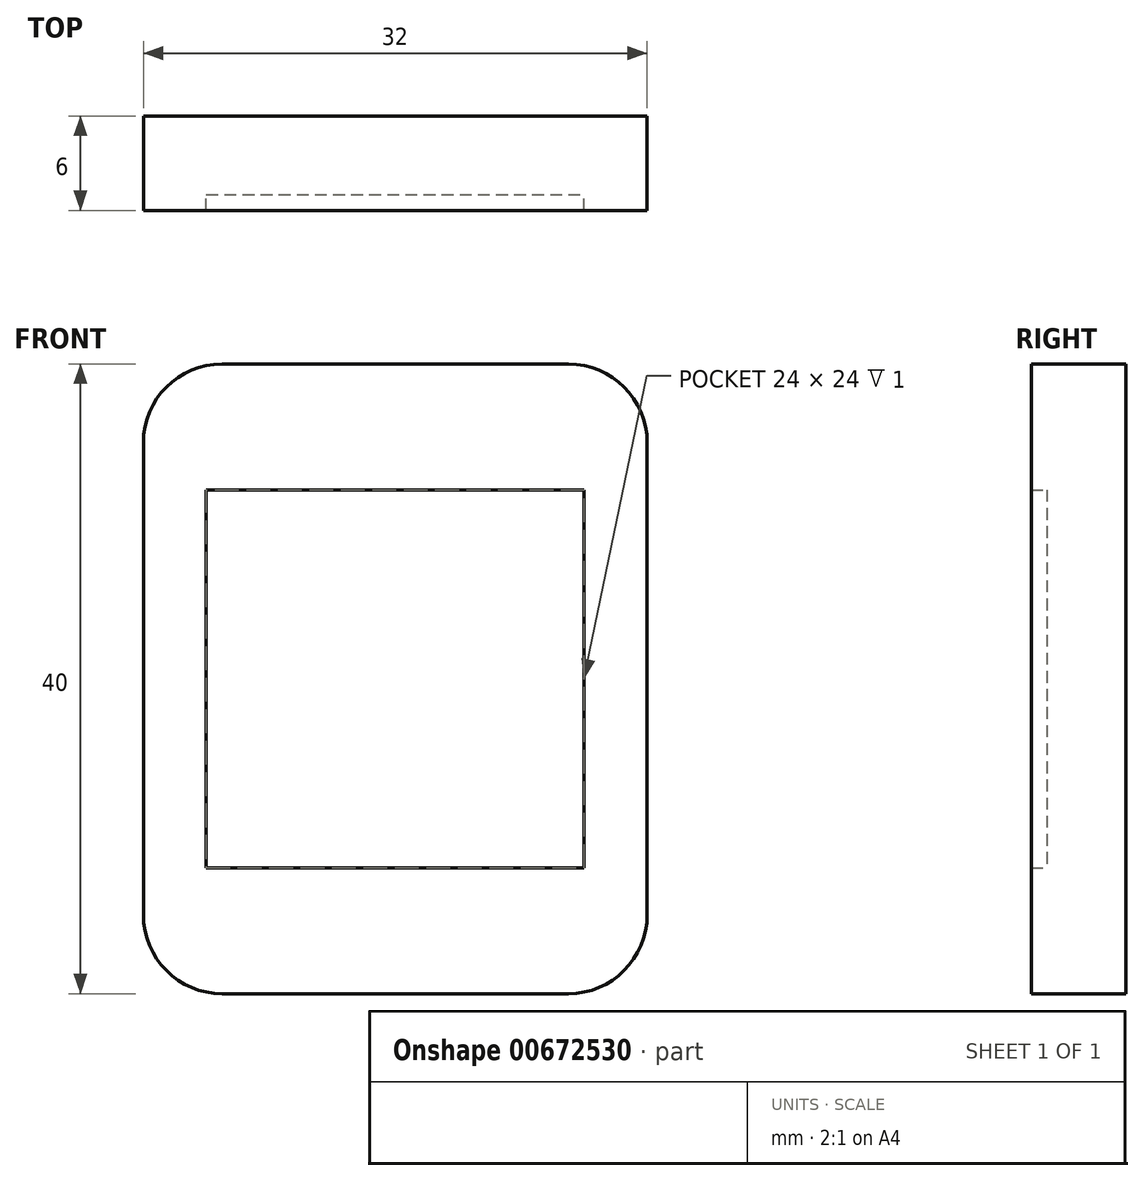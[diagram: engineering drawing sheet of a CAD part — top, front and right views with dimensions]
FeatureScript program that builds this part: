
annotation { "Feature Type Name" : "Feature", "Feature Type Description" : "" }
export const myFeature = defineFeature(function(context is Context, id is Id, definition is map)
    precondition{}
    {
        {
            var Q0;
            Q0=qCreatedBy(makeId("Front.planeOp"),FACE);
            var sketch = newSketch(context, id + "F0", { "sketchPlane" : qUnion([Q0])});
            skLineSegment(sketch, "E0.bottom", {"start": v(-12, 12) * mm, "end": v(12, 12) * mm});
            skLineSegment(sketch, "E0.top", {"start": v(-12, -12) * mm, "end": v(12, -12) * mm});
            skLineSegment(sketch, "E0.left", {"start": v(-12, 12) * mm, "end": v(-12, -12) * mm});
            skLineSegment(sketch, "E0.right", {"start": v(12, 12) * mm, "end": v(12, -12) * mm});
            skLineSegment(sketch, "E1.bottom", {"start": v(-11, 20) * mm, "end": v(11, 20) * mm});
            skLineSegment(sketch, "E1.top", {"start": v(-11, -20) * mm, "end": v(11, -20) * mm});
            skLineSegment(sketch, "E1.left", {"start": v(-16, 15) * mm, "end": v(-16, -15) * mm});
            skLineSegment(sketch, "E1.right", {"start": v(16, 15) * mm, "end": v(16, -15) * mm});
            skPoint(sketch, "E2.visualSharp", {"position": v(-16, 20) * mm});
            skArc(sketch, "E2.filletArc", {"start": v(-11, 20) * mm, "mid": v(-14.54, 18.54) * mm, "end": v(-16, 15) * mm});
            skPoint(sketch, "E3.visualSharp", {"position": v(16, 20) * mm});
            skArc(sketch, "E3.filletArc", {"start": v(16, 15) * mm, "mid": v(14.54, 18.54) * mm, "end": v(11, 20) * mm});
            skPoint(sketch, "E4.visualSharp", {"position": v(16, -20) * mm});
            skArc(sketch, "E4.filletArc", {"start": v(11, -20) * mm, "mid": v(14.54, -18.54) * mm, "end": v(16, -15) * mm});
            skPoint(sketch, "E5.visualSharp", {"position": v(-16, -20) * mm});
            skArc(sketch, "E5.filletArc", {"start": v(-16, -15) * mm, "mid": v(-14.54, -18.54) * mm, "end": v(-11, -20) * mm});
            skSolve(sketch);
        }
        {
            var Q0;
            Q0=makeQuery(id+"F0.imprint","IMPRINT",FACE,{"disambiguationData":[TD([[makeQuery(id+"F0.imprint","IMPRINT",EDGE,{"derivedFrom":sQuery(id+"F0.wireOp",EDGE,"E0.bottom")}),1.0]])]});
            extrude(context, id + "F1", {"entities" : qUnion([Q0]), "depth" : 6 * mm, "offsetDistance" : 25 * mm});
        }
        {
            var Q0;
            Q0=makeQuery(id+"F0.imprint","IMPRINT",FACE,{"disambiguationData":[TD([[makeQuery(id+"F0.imprint","IMPRINT",EDGE,{"derivedFrom":sQuery(id+"F0.wireOp",EDGE,"E0.bottom")}),-1.0]])]});
            extrude(context, id + "F2", {"entities" : qUnion([Q0]), "operationType" : NewBodyOperationType.ADD, "depth" : 5 * mm, "offsetDistance" : 25 * mm});
        }
    });
